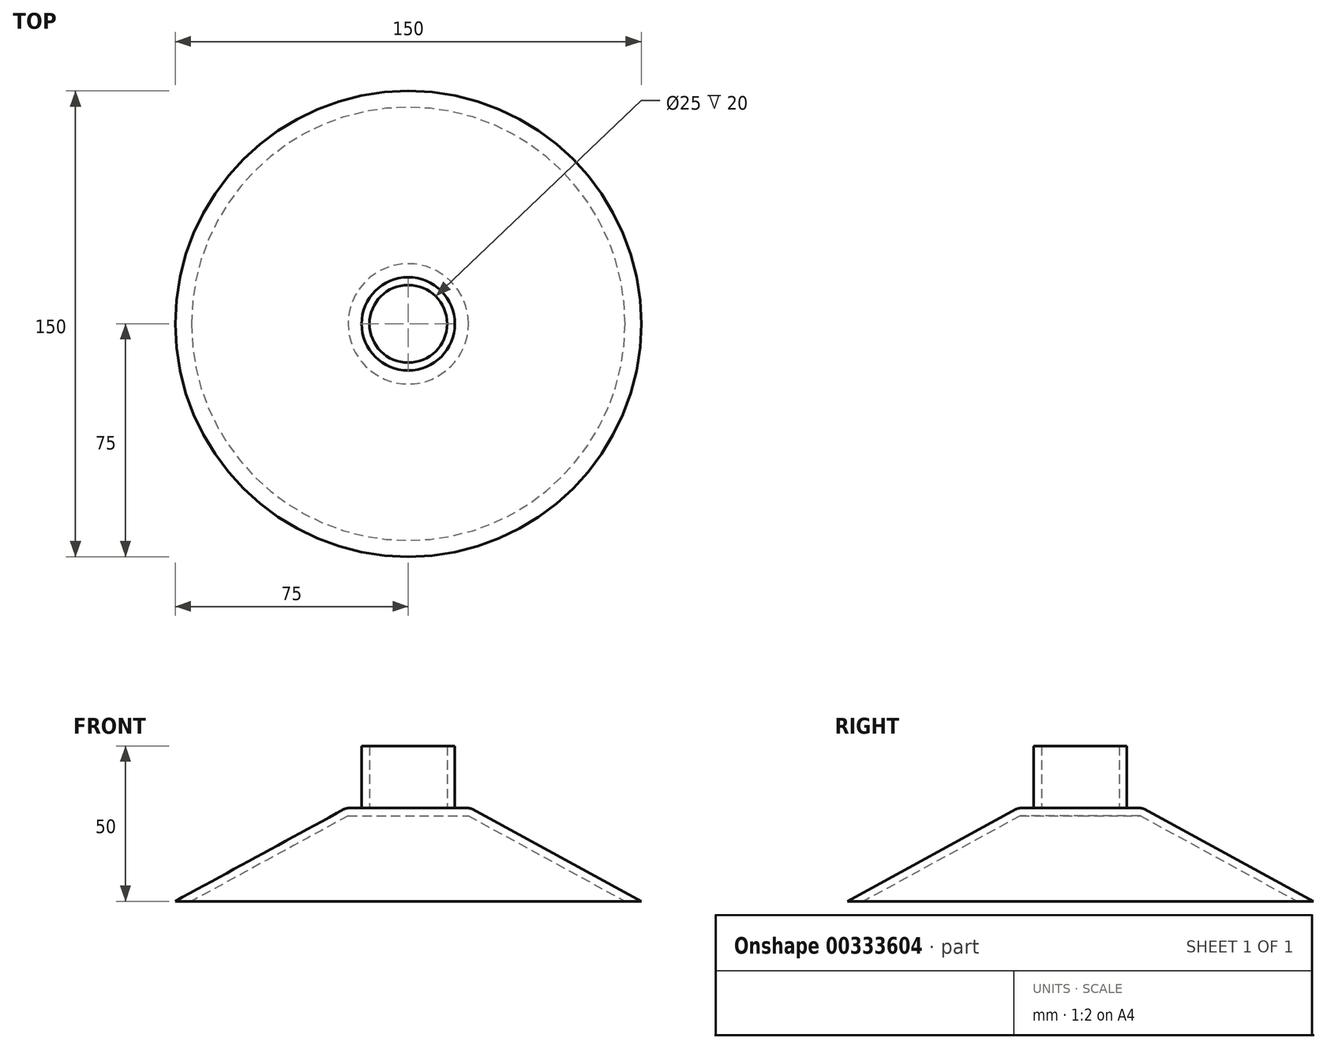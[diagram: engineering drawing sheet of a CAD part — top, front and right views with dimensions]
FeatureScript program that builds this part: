
annotation { "Feature Type Name" : "Feature", "Feature Type Description" : "" }
export const myFeature = defineFeature(function(context is Context, id is Id, definition is map)
    precondition{}
    {
        {
            var Q0;
            Q0=qCreatedBy(makeId("Right.planeOp"),FACE);
            var sketch = newSketch(context, id + "F0", { "sketchPlane" : qUnion([Q0])});
            skLineSegment(sketch, "E0", {"start": v(0, 30) * mm, "end": v(-20, 30) * mm});
            skLineSegment(sketch, "E1", {"start": v(-20, 30) * mm, "end": v(-75, 0) * mm});
            skLineSegment(sketch, "E2", {"start": v(-75, 0) * mm, "end": v(0, 0) * mm});
            skLineSegment(sketch, "E3", {"start": v(0, 0) * mm, "end": v(0, 30) * mm});
            skLineSegment(sketch, "E4", {"start": v(0, 30) * mm, "end": v(0, 45.3) * mm, "construction": true});
            skLineSegment(sketch, "E5", {"start": v(0, 0) * mm, "end": v(0, -33.7) * mm, "construction": true});
            skSolve(sketch);
        }
        {
            var Q0;
            Q0=makeQuery(id+"F0.imprint","IMPRINT",FACE,{"disambiguationData":[TD([[makeQuery(id+"F0.imprint","IMPRINT",EDGE,{"derivedFrom":sQuery(id+"F0.wireOp",EDGE,"E0")}),1.0]])]});
            var Q1;
            Q1=sQuery(id+"F0.wireOp",EDGE,"E3");
            revolve(context, id + "F1", {"entities" : qUnion([Q0]), "axis" : qUnion([Q1]), "revolveType" : RevolveType.FULL});
        }
        {
            var Q0;
            Q0=makeQuery(id+"F1.opRevolve","SWEPT_FACE",FACE,{"disambiguationData":[OSD([sQuery(id+"F0.wireOp",EDGE,"E2")])]});
            var sketch = newSketch(context, id + "F2", { "sketchPlane" : qUnion([Q0])});
            skCircle(sketch, "E6", {"center": v(0, 0) * mm, "radius": 48.5 * mm});
            skSolve(sketch);
        }
        {
            var Q0;
            Q0=makeQuery(id+"F1.opRevolve","SWEPT_FACE",FACE,{"disambiguationData":[OSD([sQuery(id+"F0.wireOp",EDGE,"E2")])]});
            shell(context, id + "F3", {"entities" : qUnion([Q0]), "thickness" : 2.5 * mm});
        }
        {
            var Q0;
            Q0=makeQuery(id+"F1.opRevolve","SWEPT_FACE",FACE,{"disambiguationData":[OSD([sQuery(id+"F0.wireOp",EDGE,"E0")])]});
            var sketch = newSketch(context, id + "F4", { "sketchPlane" : qUnion([Q0])});
            skCircle(sketch, "E7", {"center": v(0, 0) * mm, "radius": 12.5 * mm});
            skCircle(sketch, "E8", {"center": v(0, 0) * mm, "radius": 15 * mm});
            skSolve(sketch);
        }
        {
            var Q0;
            Q0=makeQuery(id+"F4.imprint","IMPRINT",FACE,{"disambiguationData":[TD([[makeQuery(id+"F4.imprint","IMPRINT",EDGE,{"derivedFrom":sQuery(id+"F4.wireOp",EDGE,"E7")}),-1.0]])]});
            extrude(context, id + "F5", {"entities" : qUnion([Q0]), "operationType" : NewBodyOperationType.ADD, "depth" : 20 * mm});
        }
        {
            var Q0;
            Q0=makeQuery(id+"F1.opRevolve","SWEPT_EDGE",EDGE,{"disambiguationData":[OSD([sQuery(id+"F0.wireOp",EDGE,"E0"),sQuery(id+"F0.wireOp",EDGE,"E1")])]});
            var Q1;
            Q1=makeQuery(id+"F5.opExtrude","CAP_EDGE",EDGE,{"disambiguationData":[OSD([sQuery(id+"F4.wireOp",EDGE,"E8")])],"isStart":true});
            fillet(context, id + "F6", {"entities" : qUnion([Q0, Q1]), "radius" : 3 * mm, "tangentPropagation" : true, "allowEdgeOverflow" : false});
        }
    });
